# Revit family: PRD_FrankeWS_SpDshs_ShowerGelDish_ACXX2021
name_source: partatom
category: Specialty Equipment
revit_build: Autodesk Revit 2018 (Build: 20190510_1515(x64)
units: mm (PartAtom-declared; Revit-internal decimal feet)

## family parameters
Cut with Voids When Loaded = No
Host = Face
OmniClass Number = 23.40.20.21.34
OmniClass Title = Soap Holders, Dispensers
Part Type = Normal
Room Calculation Point = No
Round Connector Dimension = Use Diameter
Shared = No

## types (1)
- ACXX2021
    AssetType = Fixed
    BIMObjectName = PRD_AR_SoapDishes_ShowerGelDish_ACXX2021
    Category = Pr_40_20_76_82, Soap dishes
    Color = grey
    Default Elevation = 920 mm  [stored 3.01837 ft]
    Description = Shower gel dish made of plastic, for push-in installation on F5 shower panels made of stainless steel.
    DurationUnit = year
    Features = made of plastic
    GrossWeight = 0.40 kg
    IfcExportAs = IfcFurnitureType
    IfcExportType = USERDEFINED
    IsBuiltIn = TRUE
    MainColor = grey
    Manufacturer = KWC Group AG
    ManufacturerName = KWC Group AG
    ManufacturerURL = www.kwc.com
    Material = plastic
    Model = ACXX2021
    ModelNumber = 2030057077
    ModelReference = ACXX2021
    NBSDescription = Soap dishes
    NBSReference = 45-35-72/356
    Name = Shower Gel Dish ACXX2021
    NetWeight = 0.35 kg
    NominalDepth = 89 mm  [stored 0.291995 ft]
    NominalHeight = 153 mm  [stored 0.501969 ft]
    NominalWidth = 225 mm  [stored 0.738189 ft]
    ProductInformation = https://pim.kwc.com
    Quantity = 1
    QuantityUom = Piece
    Size = 225 x 153 x 89 mm (W x H x D)
    TailorMade = No
    TrayMaterial = PRD_AR_Plastic_Grey
    TypeOfConnection = F5 shower Panel
    TypeOfMounting = push-in installation
    URL = www.kwc.com
    Uniclass2015Code = Pr_40_20_76_82
    Uniclass2015Title = Soap dishes
    Uniclass2015Version = Products v1.17
    Version = 1
    WarrantyDurationUnit = year

note: [stored X ft] marks values corroborated as IEEE doubles in the binary element streams (Revit-internal decimal feet)

## geometry (parser evidence)
native form markers: Sweep x6
no freeform markers — native parametric forms only
